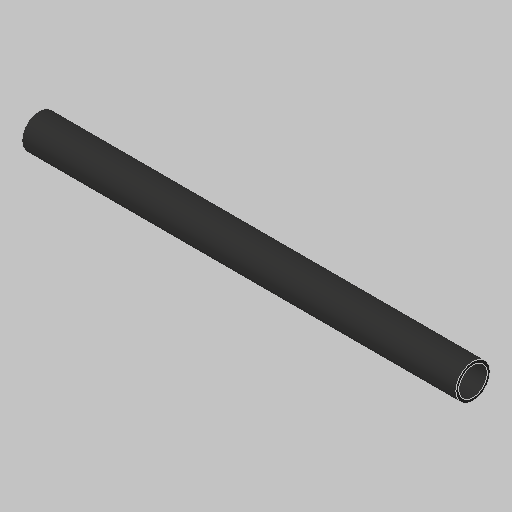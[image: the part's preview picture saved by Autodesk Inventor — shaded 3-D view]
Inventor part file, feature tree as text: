
AUTODESK INVENTOR PART (.ipt)
format: ipt  version: 2023.5 (Build 275446000, 446)  size: 88,064 bytes
history: native  units: in
note: dims shown in document units (in); Inventor stores cm internally (conversion verified against a paired STEP export)
features: extrude x1, sketch x1
ambient origin geometry x8: Origin, YZ Plane, XZ Plane, XY Plane, X Axis, Y Axis, Z Axis, Center Point
bodies: Solid1 (feature_tree)
feature tree (2):
  extrude  "Extrusion1"  Depth=19.0in TaperAngle=0.0deg
  sketch  "Sketch1"  dims[d0=1.25in d2=19.0in d3=0.0in d4=0.125in]
